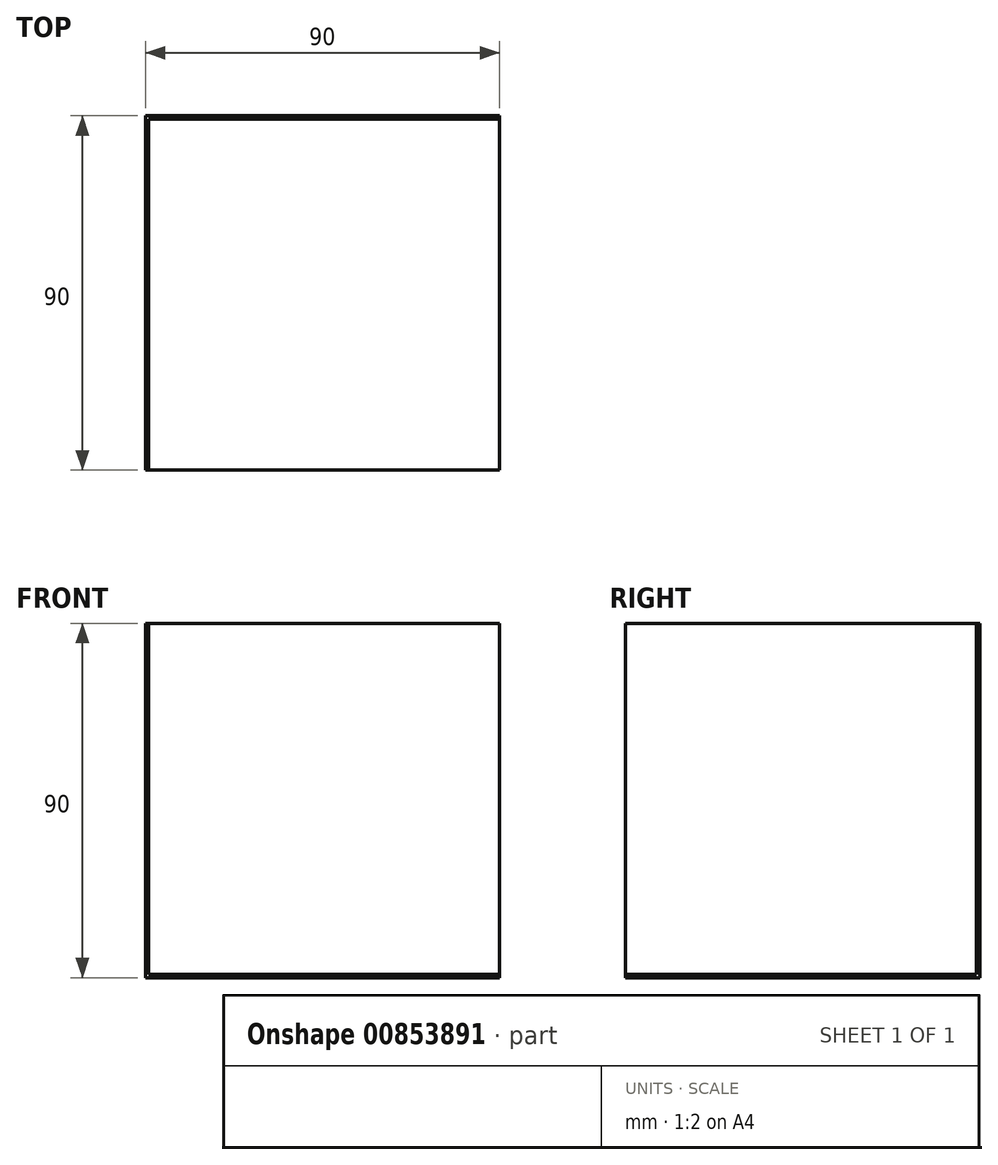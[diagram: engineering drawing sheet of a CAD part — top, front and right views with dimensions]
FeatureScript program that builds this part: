
annotation { "Feature Type Name" : "Feature", "Feature Type Description" : "" }
export const myFeature = defineFeature(function(context is Context, id is Id, definition is map)
    precondition{}
    {
        {
            var Q0;
            Q0=qCreatedBy(makeId("Top.planeOp"),FACE);
            var sketch = newSketch(context, id + "F0", { "sketchPlane" : qUnion([Q0])});
            skLineSegment(sketch, "E0.bottom", {"start": v(45, -45) * mm, "end": v(-45, -45) * mm});
            skLineSegment(sketch, "E0.top", {"start": v(45, 45) * mm, "end": v(-45, 45) * mm});
            skLineSegment(sketch, "E0.left", {"start": v(45, -45) * mm, "end": v(45, 45) * mm});
            skLineSegment(sketch, "E0.right", {"start": v(-45, -45) * mm, "end": v(-45, 45) * mm});
            skPoint(sketch, "E0.middle", {"position": v(0, 0) * mm});
            skLineSegment(sketch, "E1.bottom", {"start": v(-45, 45) * mm, "end": v(45, 45) * mm});
            skLineSegment(sketch, "E1.top", {"start": v(-45, 44.2) * mm, "end": v(45, 44.2) * mm});
            skLineSegment(sketch, "E1.left", {"start": v(-45, 45) * mm, "end": v(-45, 44.2) * mm});
            skLineSegment(sketch, "E1.right", {"start": v(45, 45) * mm, "end": v(45, 44.2) * mm});
            skLineSegment(sketch, "E2.bottom", {"start": v(-45, -45) * mm, "end": v(-44.2, -45) * mm});
            skLineSegment(sketch, "E2.top", {"start": v(-45, 44.2) * mm, "end": v(-44.2, 44.2) * mm});
            skLineSegment(sketch, "E2.left", {"start": v(-45, -45) * mm, "end": v(-45, 44.2) * mm});
            skLineSegment(sketch, "E2.right", {"start": v(-44.2, -45) * mm, "end": v(-44.2, 44.2) * mm});
            skSolve(sketch);
        }
        {
            var Q0;
            {var subQ3=sQuery(id+"F0.wireOp",EDGE,"E2.right");Q0=makeQuery(id+"F0.imprint","IMPRINT",FACE,{"disambiguationData":[TD([[makeQuery(id+"F0.imprint","IMPRINT",EDGE,{"derivedFrom":subQ3}),-1.0]])]});}
            extrude(context, id + "F1", {"entities" : qUnion([Q0]), "depth" : .80 * mm, "offsetDistance" : 25 * mm});
        }
        {
            var Q0;
            {var subQ3=sQuery(id+"F0.wireOp",EDGE,"E2.right");Q0=makeQuery(id+"F0.imprint","IMPRINT",FACE,{"disambiguationData":[TD([[makeQuery(id+"F0.imprint","IMPRINT",EDGE,{"derivedFrom":subQ3}),1.0]])]});}
            var Q1;
            {var subQ1=sQuery(id+"F0.wireOp",EDGE,"E0.top");Q1=makeQuery(id+"F0.imprint","IMPRINT",FACE,{"disambiguationData":[TD([[makeQuery(id+"F0.imprint","IMPRINT",EDGE,{"derivedFrom":subQ1}),1.0]])]});}
            extrude(context, id + "F2", {"entities" : qUnion([Q0, Q1]), "operationType" : NewBodyOperationType.ADD, "depth" : 90 * mm, "offsetDistance" : 25 * mm});
        }
    });
